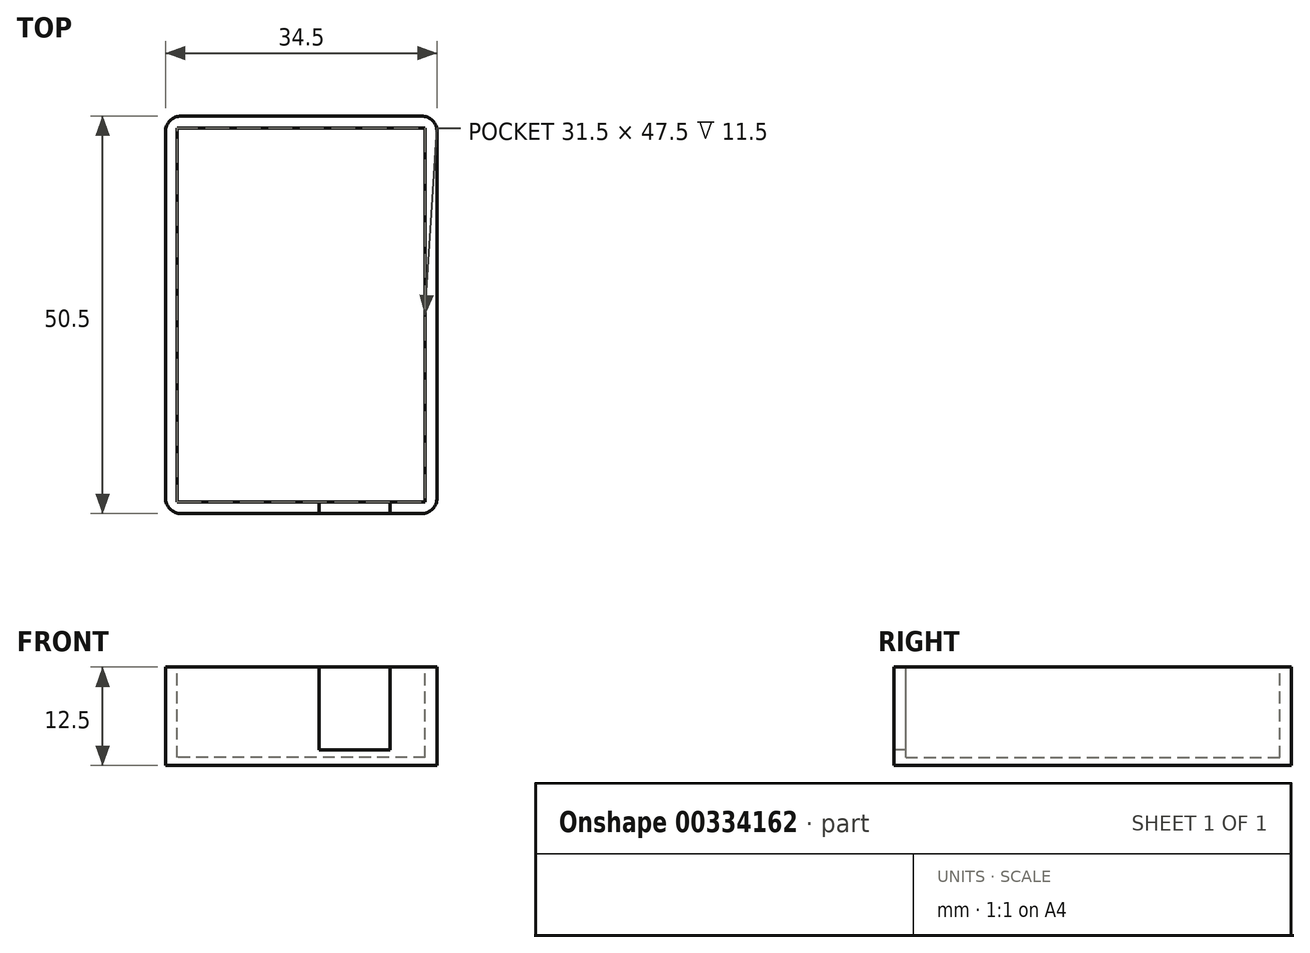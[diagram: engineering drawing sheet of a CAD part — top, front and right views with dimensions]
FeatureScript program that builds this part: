
annotation { "Feature Type Name" : "Feature", "Feature Type Description" : "" }
export const myFeature = defineFeature(function(context is Context, id is Id, definition is map)
    precondition{}
    {
        {
            var Q0;
            Q0=qCreatedBy(makeId("Top.planeOp"),FACE);
            var sketch = newSketch(context, id + "F0", { "sketchPlane" : qUnion([Q0])});
            skLineSegment(sketch, "E0.bottom", {"start": v(17.25, -25.25) * mm, "end": v(-17.25, -25.25) * mm});
            skLineSegment(sketch, "E0.top", {"start": v(17.25, 25.25) * mm, "end": v(-17.25, 25.25) * mm});
            skLineSegment(sketch, "E0.left", {"start": v(17.25, -25.25) * mm, "end": v(17.25, 25.25) * mm});
            skLineSegment(sketch, "E0.right", {"start": v(-17.25, -25.25) * mm, "end": v(-17.25, 25.25) * mm});
            skPoint(sketch, "E0.middle", {"position": v(0, 0) * mm});
            skSolve(sketch);
        }
        {
            var Q0;
            Q0 = qSketchRegion(id + "F0", true);
            extrude(context, id + "F1", {"entities" : qUnion([Q0]), "depth" : 12.5 * mm});
        }
        {
            var Q0;
            Q0=makeQuery(id+"F1.opExtrude","CAP_FACE",FACE,{"disambiguationData":[OSD([sQuery(id+"F0.wireOp",EDGE,"E0.bottom"),sQuery(id+"F0.wireOp",EDGE,"E0.top"),sQuery(id+"F0.wireOp",EDGE,"E0.left"),sQuery(id+"F0.wireOp",EDGE,"E0.right")])],"isStart":false});
            var sketch = newSketch(context, id + "F2", { "sketchPlane" : qUnion([Q0])});
            skLineSegment(sketch, "E1.bottom", {"start": v(15.75, -23.75) * mm, "end": v(-15.75, -23.75) * mm});
            skLineSegment(sketch, "E1.top", {"start": v(15.75, 23.75) * mm, "end": v(-15.75, 23.75) * mm});
            skLineSegment(sketch, "E1.left", {"start": v(15.75, -23.75) * mm, "end": v(15.75, 23.75) * mm});
            skLineSegment(sketch, "E1.right", {"start": v(-15.75, -23.75) * mm, "end": v(-15.75, 23.75) * mm});
            skPoint(sketch, "E1.middle", {"position": v(0, 0) * mm});
            skSolve(sketch);
        }
        {
            var Q0;
            Q0 = qSketchRegion(id + "F2", true);
            extrude(context, id + "F3", {"entities" : qUnion([Q0]), "operationType" : NewBodyOperationType.REMOVE, "oppositeDirection" : true, "depth" : 11.5 * mm});
        }
        {
            var Q0;
            Q0=makeQuery(id+"F1.opExtrude","SWEPT_FACE",FACE,{"disambiguationData":[OSD([sQuery(id+"F0.wireOp",EDGE,"E0.bottom")])]});
            var sketch = newSketch(context, id + "F4", { "sketchPlane" : qUnion([Q0])});
            skLineSegment(sketch, "E2.bottom", {"start": v(2.25, 12.5) * mm, "end": v(11.25, 12.5) * mm});
            skLineSegment(sketch, "E2.top", {"start": v(2.25, 2) * mm, "end": v(11.25, 2) * mm});
            skLineSegment(sketch, "E2.left", {"start": v(2.25, 12.5) * mm, "end": v(2.25, 2) * mm});
            skLineSegment(sketch, "E2.right", {"start": v(11.25, 12.5) * mm, "end": v(11.25, 2) * mm});
            skSolve(sketch);
        }
        {
            var Q0;
            Q0 = qSketchRegion(id + "F4", true);
            extrude(context, id + "F5", {"entities" : qUnion([Q0]), "operationType" : NewBodyOperationType.REMOVE, "oppositeDirection" : true, "depth" : 25 * mm});
        }
        {
            var Q0;
            Q0=makeQuery(id+"F1.opExtrude","SWEPT_EDGE",EDGE,{"disambiguationData":[OSD([sQuery(id+"F0.wireOp",EDGE,"E0.bottom"),sQuery(id+"F0.wireOp",EDGE,"E0.left")])]});
            var Q1;
            Q1=makeQuery(id+"F1.opExtrude","SWEPT_EDGE",EDGE,{"disambiguationData":[OSD([sQuery(id+"F0.wireOp",EDGE,"E0.top"),sQuery(id+"F0.wireOp",EDGE,"E0.left")])]});
            var Q2;
            Q2=makeQuery(id+"F1.opExtrude","SWEPT_EDGE",EDGE,{"disambiguationData":[OSD([sQuery(id+"F0.wireOp",EDGE,"E0.top"),sQuery(id+"F0.wireOp",EDGE,"E0.right")])]});
            var Q3;
            Q3=makeQuery(id+"F1.opExtrude","SWEPT_EDGE",EDGE,{"disambiguationData":[OSD([sQuery(id+"F0.wireOp",EDGE,"E0.bottom"),sQuery(id+"F0.wireOp",EDGE,"E0.right")])]});
            fillet(context, id + "F6", {"entities" : qUnion([Q0, Q1, Q2, Q3]), "radius" : 2 * mm, "tangentPropagation" : true, "allowEdgeOverflow" : false});
        }
    });
